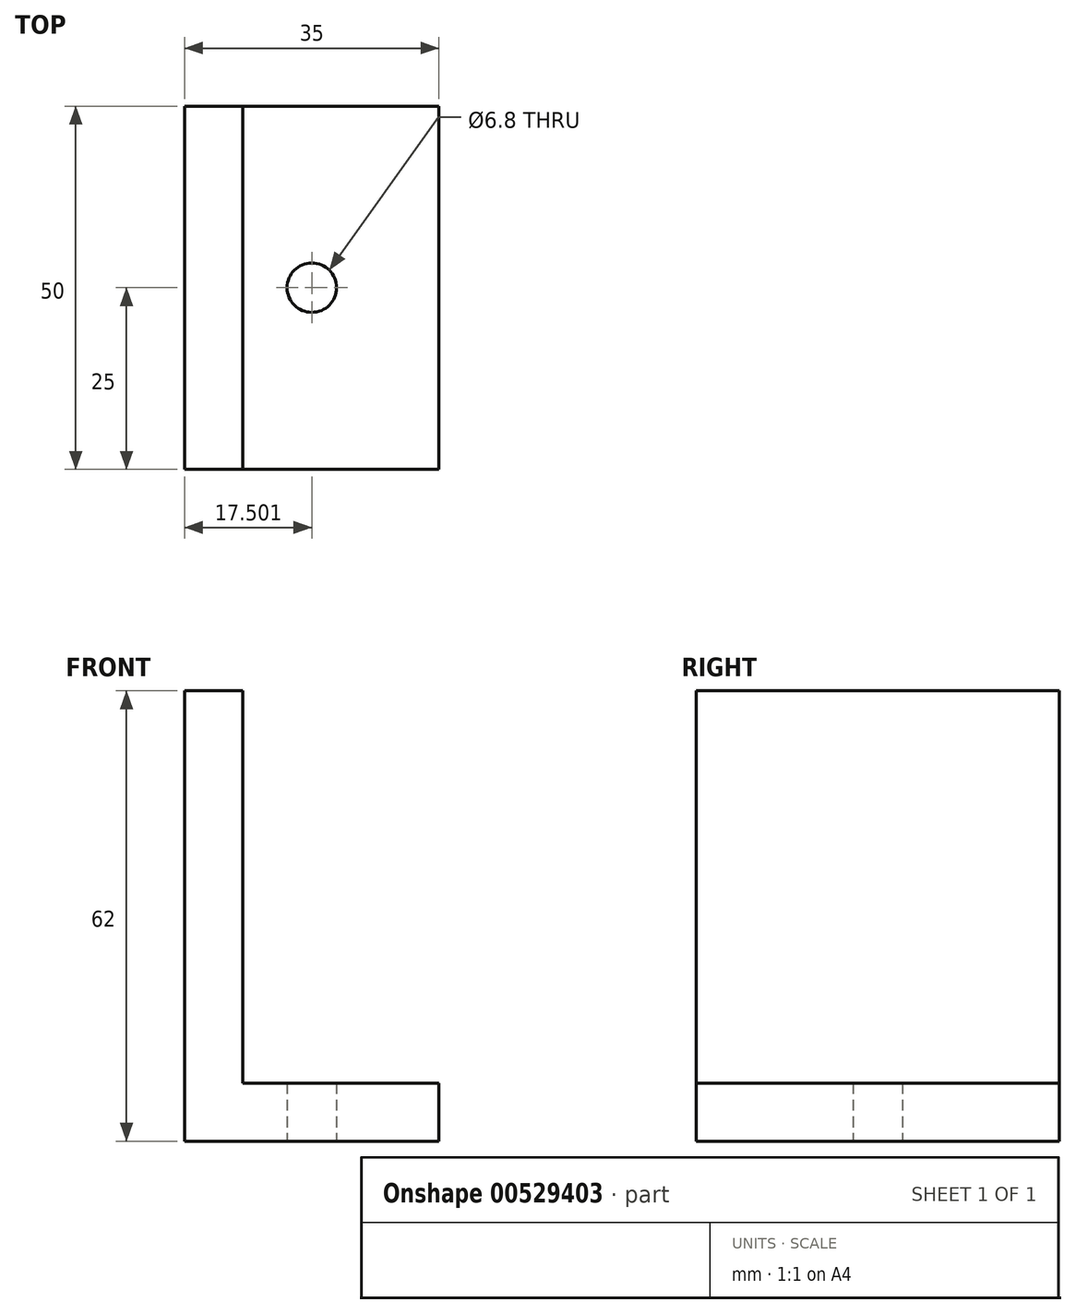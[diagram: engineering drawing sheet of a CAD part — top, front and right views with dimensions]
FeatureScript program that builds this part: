
annotation { "Feature Type Name" : "Feature", "Feature Type Description" : "" }
export const myFeature = defineFeature(function(context is Context, id is Id, definition is map)
    precondition{}
    {
        {
            var Q0;
            Q0=qCreatedBy(makeId("Front.planeOp"),FACE);
            var sketch = newSketch(context, id + "F0", { "sketchPlane" : qUnion([Q0])});
            skLineSegment(sketch, "E0.bottom", {"start": v(-8.33, 1.1) * mm, "end": v(18.67, 1.1) * mm});
            skLineSegment(sketch, "E0.top", {"start": v(-8.33, -6.9) * mm, "end": v(18.67, -6.9) * mm});
            skLineSegment(sketch, "E0.left", {"start": v(-8.33, 1.1) * mm, "end": v(-8.33, -6.9) * mm});
            skLineSegment(sketch, "E0.right", {"start": v(18.67, 1.1) * mm, "end": v(18.67, -6.9) * mm});
            skLineSegment(sketch, "E1.left", {"start": v(18.67, -6.9) * mm, "end": v(18.67, -6.9) * mm});
            skLineSegment(sketch, "E2.bottom", {"start": v(-8.33, -6.9) * mm, "end": v(-16.33, -6.9) * mm});
            skLineSegment(sketch, "E2.top", {"start": v(-8.33, 55.1) * mm, "end": v(-16.33, 55.1) * mm});
            skLineSegment(sketch, "E2.left", {"start": v(-8.33, -6.9) * mm, "end": v(-8.33, 55.1) * mm});
            skLineSegment(sketch, "E2.right", {"start": v(-16.33, -6.9) * mm, "end": v(-16.33, 55.1) * mm});
            skSolve(sketch);
        }
        {
            var Q0;
            {var subQ0=sQuery(id+"F0.wireOp",EDGE,"E0.bottom");Q0=makeQuery(id+"F0.imprint","IMPRINT",FACE,{"disambiguationData":[TD([[makeQuery(id+"F0.imprint","IMPRINT",EDGE,{"derivedFrom":subQ0}),-1.0]])]});}
            var Q1;
            {var subQ3=sQuery(id+"F0.wireOp",EDGE,"E2.bottom");Q1=makeQuery(id+"F0.imprint","IMPRINT",FACE,{"disambiguationData":[TD([[makeQuery(id+"F0.imprint","IMPRINT",EDGE,{"derivedFrom":subQ3}),-1.0]])]});}
            extrude(context, id + "F1", {"entities" : qUnion([Q0, Q1]), "depth" : 50 * mm, "offsetDistance" : 25 * mm});
        }
        {
            var Q0;
            Q0=makeQuery(id+"F1.opExtrude","SWEPT_FACE",FACE,{"disambiguationData":[OSD([sQuery(id+"F0.wireOp",EDGE,"E0.top"),sQuery(id+"F0.wireOp",EDGE,"E2.bottom")])]});
            var sketch = newSketch(context, id + "F2", { "sketchPlane" : qUnion([Q0])});
            skLineSegment(sketch, "E3", {"start": v(-16.33, 25) * mm, "end": v(18.67, 25) * mm});
            skLineSegment(sketch, "E4", {"start": v(1.17, 50) * mm, "end": v(1.17, 0) * mm});
            skPoint(sketch, "E5", {"position": v(1.17, 25) * mm});
            skSolve(sketch);
        }
        {
            var Q0;
            Q0=sQuery(id+"F2.wireOp",VERTEX,"E5");
            var Q1;
            Q1=makeQuery(id+"F1.opExtrude","SWEPT_BODY",BODY,{"disambiguationData":[OSD([sQuery(id+"F0.wireOp",EDGE,"E0.bottom"),sQuery(id+"F0.wireOp",EDGE,"E0.top"),sQuery(id+"F0.wireOp",EDGE,"E0.right"),sQuery(id+"F0.wireOp",EDGE,"E2.bottom"),sQuery(id+"F0.wireOp",EDGE,"E2.top"),sQuery(id+"F0.wireOp",EDGE,"E2.left"),sQuery(id+"F0.wireOp",EDGE,"E2.right")])]});
            hole(context, id + "F3", {"style" : HoleStyle.SIMPLE, "endStyle" : HoleEndStyle.THROUGH, "standardTappedOrClearance" : lookupTablePath({ "standard" : "ISO", "engagement" : "75%", "pitch" : "1.25 mm", "size" : "M8", "type" : "Tapped" }), "standardBlindInLast" : lookupTablePath({ "standard" : "ISO", "engagement" : "75%", "pitch" : "1.25 mm", "size" : "M8", "type" : "Tapped" }), "holeDiameter" : 6.8 * mm, "showTappedDepth" : true, "isTappedThrough" : true, "tappedDepth" : 12 * mm, "tapClearance" : 3, "locations" : qUnion([Q0]), "scope" : qUnion([Q1]), "majorDiameter" : 8 * mm});
        }
    });
